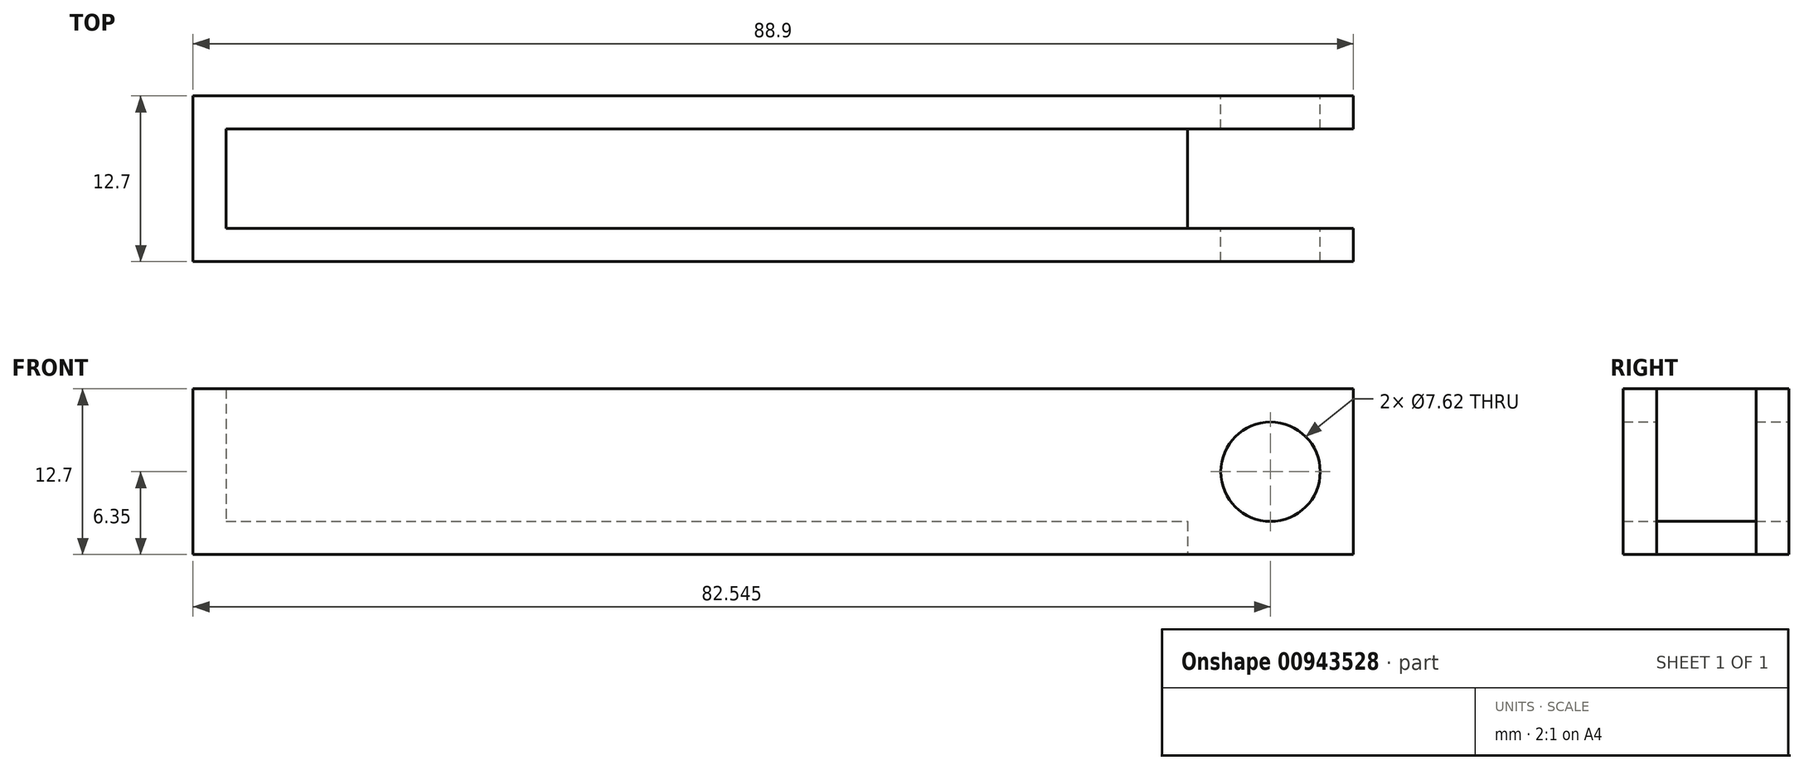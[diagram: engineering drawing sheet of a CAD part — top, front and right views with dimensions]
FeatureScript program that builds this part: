
annotation { "Feature Type Name" : "Feature", "Feature Type Description" : "" }
export const myFeature = defineFeature(function(context is Context, id is Id, definition is map)
    precondition{}
    {
        {
            var Q0;
            Q0=qCreatedBy(makeId("Top.planeOp"),FACE);
            var sketch = newSketch(context, id + "F0", { "sketchPlane" : qUnion([Q0])});
            skLineSegment(sketch, "E0.bottom", {"start": v(-40.56, 26.59) * mm, "end": v(48.34, 26.59) * mm});
            skLineSegment(sketch, "E0.top", {"start": v(-40.56, 13.89) * mm, "end": v(48.34, 13.89) * mm});
            skLineSegment(sketch, "E0.left", {"start": v(-40.56, 26.59) * mm, "end": v(-40.56, 13.89) * mm});
            skLineSegment(sketch, "E0.right", {"start": v(48.34, 26.59) * mm, "end": v(48.34, 13.89) * mm});
            skSolve(sketch);
        }
        {
            var Q0;
            Q0=makeQuery(id+"F0.imprint","IMPRINT",FACE,{"disambiguationData":[TD([[makeQuery(id+"F0.imprint","IMPRINT",EDGE,{"derivedFrom":sQuery(id+"F0.wireOp",EDGE,"E0.bottom")}),-1.0]])]});
            extrude(context, id + "F1", {"entities" : qUnion([Q0]), "depth" : 12.7 * mm, "offsetDistance" : 25.4 * mm});
        }
        {
            var Q0;
            Q0=makeQuery(id+"F1.opExtrude","CAP_FACE",FACE,{"disambiguationData":[OSD([sQuery(id+"F0.wireOp",EDGE,"E0.bottom"),sQuery(id+"F0.wireOp",EDGE,"E0.top"),sQuery(id+"F0.wireOp",EDGE,"E0.left"),sQuery(id+"F0.wireOp",EDGE,"E0.right")])],"isStart":false});
            var sketch = newSketch(context, id + "F2", { "sketchPlane" : qUnion([Q0])});
            skLineSegment(sketch, "E1.bottom", {"start": v(-38.02, 24.05) * mm, "end": v(45.8, 24.05) * mm});
            skLineSegment(sketch, "E1.top", {"start": v(-38.02, 16.43) * mm, "end": v(45.8, 16.43) * mm});
            skLineSegment(sketch, "E1.left", {"start": v(-38.02, 24.05) * mm, "end": v(-38.02, 16.43) * mm});
            skLineSegment(sketch, "E1.right", {"start": v(45.8, 24.05) * mm, "end": v(45.8, 16.43) * mm});
            skSolve(sketch);
        }
        {
            var Q0;
            Q0=makeQuery(id+"F2.imprint","IMPRINT",FACE,{"disambiguationData":[TD([[makeQuery(id+"F2.imprint","IMPRINT",EDGE,{"derivedFrom":sQuery(id+"F2.wireOp",EDGE,"E1.bottom")}),-1.0]])]});
            extrude(context, id + "F3", {"entities" : qUnion([Q0]), "operationType" : NewBodyOperationType.ADD, "depth" : -10.16 * mm, "offsetDistance" : 25.4 * mm});
        }
        {
            var Q0;
            Q0=makeQuery(id+"F1.opExtrude","CAP_FACE",FACE,{"disambiguationData":[OSD([sQuery(id+"F0.wireOp",EDGE,"E0.bottom"),sQuery(id+"F0.wireOp",EDGE,"E0.top"),sQuery(id+"F0.wireOp",EDGE,"E0.left"),sQuery(id+"F0.wireOp",EDGE,"E0.right")])],"isStart":false});
            shell(context, id + "F4", {"entities" : qUnion([Q0]), "thickness" : 2.54 * mm});
        }
        {
            var Q0;
            Q0=makeQuery(id+"F1.opExtrude","CAP_FACE",FACE,{"disambiguationData":[OSD([sQuery(id+"F0.wireOp",EDGE,"E0.bottom"),sQuery(id+"F0.wireOp",EDGE,"E0.top"),sQuery(id+"F0.wireOp",EDGE,"E0.left"),sQuery(id+"F0.wireOp",EDGE,"E0.right")])],"isStart":true});
            var sketch = newSketch(context, id + "F5", { "sketchPlane" : qUnion([Q0])});
            skLineSegment(sketch, "E2.bottom", {"start": v(48.34, -24.05) * mm, "end": v(35.64, -24.05) * mm});
            skLineSegment(sketch, "E2.top", {"start": v(48.34, -16.43) * mm, "end": v(35.64, -16.43) * mm});
            skLineSegment(sketch, "E2.left", {"start": v(48.34, -24.05) * mm, "end": v(48.34, -16.43) * mm});
            skLineSegment(sketch, "E2.right", {"start": v(35.64, -24.05) * mm, "end": v(35.64, -16.43) * mm});
            skSolve(sketch);
        }
        {
            var Q0;
            Q0=makeQuery(id+"F5.imprint","IMPRINT",FACE,{"disambiguationData":[TD([[makeQuery(id+"F5.imprint","IMPRINT",EDGE,{"derivedFrom":sQuery(id+"F5.wireOp",EDGE,"E2.bottom")}),-1.0]])]});
            extrude(context, id + "F6", {"entities" : qUnion([Q0]), "operationType" : NewBodyOperationType.REMOVE, "oppositeDirection" : true, "depth" : 25.4 * mm, "offsetDistance" : 25.4 * mm});
        }
        {
            var Q0;
            Q0=makeQuery(id+"F1.opExtrude","SWEPT_FACE",FACE,{"disambiguationData":[OSD([sQuery(id+"F0.wireOp",EDGE,"E0.bottom")])]});
            var sketch = newSketch(context, id + "F7", { "sketchPlane" : qUnion([Q0])});
            skLineSegment(sketch, "E3.bottom", {"start": v(-35.64, 0) * mm, "end": v(-48.34, 0) * mm});
            skLineSegment(sketch, "E3.top", {"start": v(-35.64, 12.7) * mm, "end": v(-48.34, 12.7) * mm});
            skLineSegment(sketch, "E3.left", {"start": v(-35.64, 0) * mm, "end": v(-35.64, 12.7) * mm});
            skLineSegment(sketch, "E3.right", {"start": v(-48.34, 0) * mm, "end": v(-48.34, 12.7) * mm});
            skCircle(sketch, "E4", {"center": v(-41.99, 6.35) * mm, "radius": 3.81 * mm});
            skPoint(sketch, "E4.centerSnap0", {"position": v(-48.34, 6.35) * mm});
            skSolve(sketch);
        }
        {
            var Q0;
            Q0=makeQuery(id+"F7.imprint","IMPRINT",FACE,{"disambiguationData":[TD([[makeQuery(id+"F7.imprint","IMPRINT",EDGE,{"derivedFrom":sQuery(id+"F7.wireOp",EDGE,"E4")}),1.0]])]});
            extrude(context, id + "F8", {"entities" : qUnion([Q0]), "operationType" : NewBodyOperationType.REMOVE, "oppositeDirection" : true, "depth" : 25.4 * mm, "offsetDistance" : 25.4 * mm});
        }
    });
